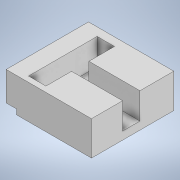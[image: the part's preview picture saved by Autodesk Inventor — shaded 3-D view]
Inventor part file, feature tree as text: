
AUTODESK INVENTOR PART (.ipt)
format: ipt  version: 2022.3 (Build 263350000, 350)  size: 373,248 bytes
history: native  units: mm
features: extrude x8, sketch x6, thicken_offset x3, hole x1, projected_geometry x1
ambient origin geometry x8: Origin, YZ Plane, XZ Plane, XY Plane, X Axis, Y Axis, Z Axis, Center Point
bodies: Solid1 (feature_tree)
feature tree (19):
  sketch  "Sketch1"  dims[d1=200.0mm d2=35.0mm]
  extrude  "Extrusion1"  Depth=35.0mm
  extrude  "Extrusion2"  Depth=5.0mm
  extrude  "Extrusion3"  Depth=30.0mm
  extrude  "Extrusion4"  Depth=10.0mm TaperAngle=0.0deg
  sketch  "Sketch3"  dims[d5=20.0mm d6=30.0mm d8=40.0mm d9=30.0mm d11=40.0mm]
  extrude  "Extrusion6"  Depth=22.0mm
  extrude  "Extrusion7"  Depth=1.5mm TaperAngle=0.0deg
  hole  "Hole1"  [1 undecoded]
  extrude  "Extrusion8"  TaperAngle=120.0deg  [1 undecoded]
  thicken_offset  "Thicken1"
  thicken_offset  "Thicken2"
  extrude  "Extrusion9"  Depth=10.0mm
  thicken_offset  "Thicken3"
  sketch  "Sketch2"  dims[d3=5.0mm d4=5.0mm]
  projected_geometry  "Projected Loop1"
  sketch  "Sketch4"  dims[d14=10.0mm d15=0.0mm d16=10.0mm d17=0.0mm]
  sketch  "Sketch5"  dims[d18=2.5mm d19=0.0mm d20=22.0mm]
  sketch  "Sketch6"  dims[d21=3.0mm d22=1.5mm d23=0.0mm d24=15.0mm d25=120.0deg d26=10.0mm d27=5.0mm d28=20.0mm d29=90.0deg d30=5.0mm d31=2.5mm d32=5.0mm d33=20.0mm d35=120.0deg d37=30.0mm d39=40.0mm d40=30.0mm d42=40.0mm d45=30.0mm d47=40.0mm d48=30.0mm d50=40.0mm d55=10.0mm d56=0.0mm d57=10.0mm d58=0.0mm d59=40.0mm d60=2.2mm d61=6.0mm d62=3.1mm d63=4.1mm d64=90.0deg d65=2.2mm d66=0.0mm d67=10.0mm d68=0.0mm d69=0.05mm d70=0.1mm d71=0.2mm d72=0.2mm d73=10.0mm d74=0.0mm d75=0.2mm d76=0.2mm d77=0.75mm d78=0.375mm]
note: 2 required parameter values undecoded (feature->parameter linkage not recoverable at this tier; creation-order binding heuristic only, values carry confidence <= 0.55)
